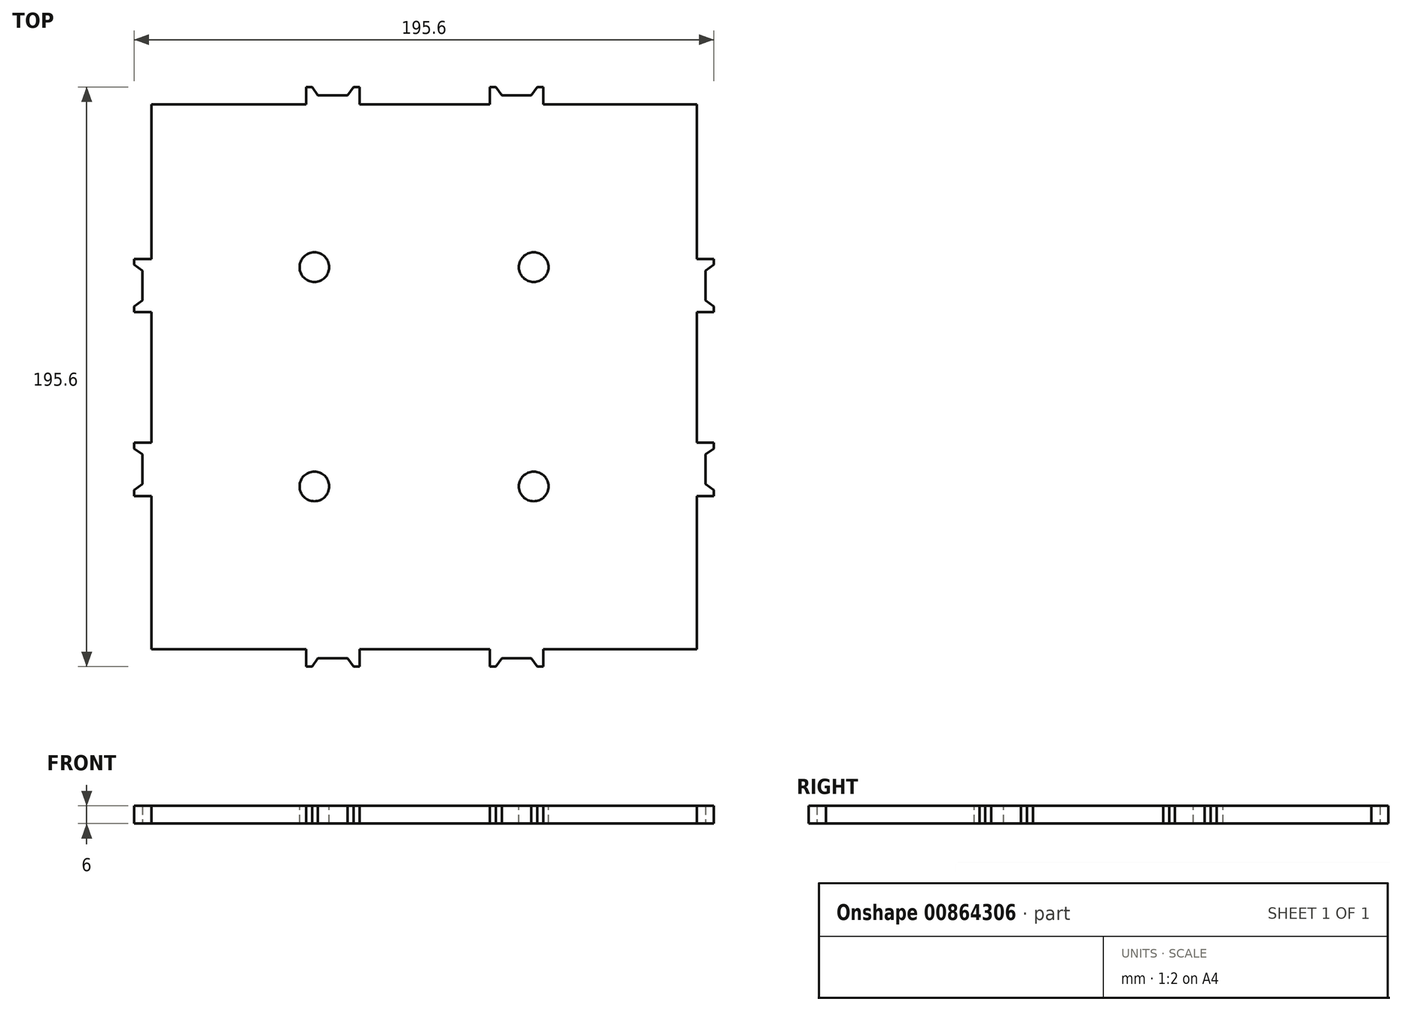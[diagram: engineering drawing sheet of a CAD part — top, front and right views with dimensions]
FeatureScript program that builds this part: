
annotation { "Feature Type Name" : "Feature", "Feature Type Description" : "" }
export const myFeature = defineFeature(function(context is Context, id is Id, definition is map)
    precondition{}
    {
        {
            var Q0;
            Q0=qCreatedBy(makeId("Top.planeOp"),FACE);
            var sketch = newSketch(context, id + "F0", { "sketchPlane" : qUnion([Q0])});
            skLineSegment(sketch, "E0.bottom", {"start": v(-124.48, 94.97) * mm, "end": v(-72.28, 94.97) * mm});
            skLineSegment(sketch, "E0.top", {"start": v(-124.48, -89.03) * mm, "end": v(-72.28, -89.03) * mm});
            skLineSegment(sketch, "E0.left", {"start": v(-124.48, 94.97) * mm, "end": v(-124.48, 42.77) * mm});
            skLineSegment(sketch, "E0.right", {"start": v(59.52, 94.97) * mm, "end": v(59.52, 42.77) * mm});
            skLineSegment(sketch, "E1", {"start": v(-72.28, 94.97) * mm, "end": v(-72.28, 100.77) * mm});
            skLineSegment(sketch, "E2", {"start": v(-72.28, 100.77) * mm, "end": v(-70.28, 100.77) * mm});
            skLineSegment(sketch, "E3", {"start": v(-70.28, 100.77) * mm, "end": v(-68.28, 97.97) * mm});
            skLineSegment(sketch, "E4", {"start": v(-68.28, 97.97) * mm, "end": v(-58.28, 97.97) * mm});
            skLineSegment(sketch, "E5", {"start": v(-58.28, 97.97) * mm, "end": v(-56.28, 100.77) * mm});
            skLineSegment(sketch, "E6", {"start": v(-56.28, 100.77) * mm, "end": v(-54.28, 100.77) * mm});
            skLineSegment(sketch, "E7", {"start": v(-54.28, 100.77) * mm, "end": v(-54.28, 94.97) * mm});
            skLineSegment(sketch, "E8.trimOffspring", {"start": v(-54.28, 94.97) * mm, "end": v(-10.28, 94.97) * mm});
            skLineSegment(sketch, "E9", {"start": v(-10.28, 94.97) * mm, "end": v(-10.28, 100.77) * mm});
            skLineSegment(sketch, "E10", {"start": v(-10.28, 100.77) * mm, "end": v(-8.28, 100.77) * mm});
            skLineSegment(sketch, "E11", {"start": v(-8.28, 100.77) * mm, "end": v(-6.28, 97.97) * mm});
            skLineSegment(sketch, "E12", {"start": v(-6.28, 97.97) * mm, "end": v(3.72, 97.97) * mm});
            skLineSegment(sketch, "E13", {"start": v(3.72, 97.97) * mm, "end": v(5.72, 100.77) * mm});
            skLineSegment(sketch, "E14", {"start": v(5.72, 100.77) * mm, "end": v(7.72, 100.77) * mm});
            skLineSegment(sketch, "E15", {"start": v(7.72, 100.77) * mm, "end": v(7.72, 94.97) * mm});
            skLineSegment(sketch, "E16.trimOffspring", {"start": v(7.72, 94.97) * mm, "end": v(59.52, 94.97) * mm});
            skLineSegment(sketch, "E17", {"start": v(59.52, 42.77) * mm, "end": v(65.32, 42.77) * mm});
            skLineSegment(sketch, "E18", {"start": v(65.32, 42.77) * mm, "end": v(65.32, 40.77) * mm});
            skLineSegment(sketch, "E19", {"start": v(65.32, 40.77) * mm, "end": v(62.52, 38.77) * mm});
            skLineSegment(sketch, "E20", {"start": v(62.52, 38.77) * mm, "end": v(62.52, 28.77) * mm});
            skLineSegment(sketch, "E21", {"start": v(62.52, 28.77) * mm, "end": v(65.32, 26.77) * mm});
            skLineSegment(sketch, "E22", {"start": v(65.32, 26.77) * mm, "end": v(65.32, 24.77) * mm});
            skLineSegment(sketch, "E23", {"start": v(65.32, 24.77) * mm, "end": v(59.52, 24.77) * mm});
            skLineSegment(sketch, "E24", {"start": v(59.52, -19.23) * mm, "end": v(65.32, -19.23) * mm});
            skLineSegment(sketch, "E25", {"start": v(65.32, -19.23) * mm, "end": v(65.32, -21.23) * mm});
            skLineSegment(sketch, "E26", {"start": v(65.32, -21.23) * mm, "end": v(62.52, -23.23) * mm});
            skLineSegment(sketch, "E27", {"start": v(62.52, -23.23) * mm, "end": v(62.52, -33.23) * mm});
            skLineSegment(sketch, "E28", {"start": v(62.52, -33.23) * mm, "end": v(65.32, -35.23) * mm});
            skLineSegment(sketch, "E29", {"start": v(65.32, -35.23) * mm, "end": v(65.32, -37.23) * mm});
            skLineSegment(sketch, "E30", {"start": v(65.32, -37.23) * mm, "end": v(59.52, -37.23) * mm});
            skLineSegment(sketch, "E31.trimOffspring", {"start": v(59.52, 24.77) * mm, "end": v(59.52, -19.23) * mm});
            skLineSegment(sketch, "E32.trimOffspring", {"start": v(59.52, -37.23) * mm, "end": v(59.52, -89.03) * mm});
            skLineSegment(sketch, "E33", {"start": v(-72.28, -89.03) * mm, "end": v(-72.28, -94.83) * mm});
            skLineSegment(sketch, "E34", {"start": v(-72.28, -94.83) * mm, "end": v(-70.28, -94.83) * mm});
            skLineSegment(sketch, "E35", {"start": v(-70.28, -94.83) * mm, "end": v(-68.28, -92.03) * mm});
            skLineSegment(sketch, "E36", {"start": v(-68.28, -92.03) * mm, "end": v(-58.28, -92.03) * mm});
            skLineSegment(sketch, "E37", {"start": v(-58.28, -92.03) * mm, "end": v(-56.28, -94.83) * mm});
            skLineSegment(sketch, "E38", {"start": v(-56.28, -94.83) * mm, "end": v(-54.28, -94.83) * mm});
            skLineSegment(sketch, "E39", {"start": v(-54.28, -94.83) * mm, "end": v(-54.28, -89.03) * mm});
            skLineSegment(sketch, "E40", {"start": v(-10.28, -89.03) * mm, "end": v(-10.28, -94.83) * mm});
            skLineSegment(sketch, "E41", {"start": v(-10.28, -94.83) * mm, "end": v(-8.28, -94.83) * mm});
            skLineSegment(sketch, "E42", {"start": v(-8.28, -94.83) * mm, "end": v(-6.28, -92.03) * mm});
            skLineSegment(sketch, "E43", {"start": v(-6.28, -92.03) * mm, "end": v(3.72, -92.03) * mm});
            skLineSegment(sketch, "E44", {"start": v(3.72, -92.03) * mm, "end": v(5.72, -94.83) * mm});
            skLineSegment(sketch, "E45", {"start": v(5.72, -94.83) * mm, "end": v(7.72, -94.83) * mm});
            skLineSegment(sketch, "E46", {"start": v(7.72, -94.83) * mm, "end": v(7.72, -89.03) * mm});
            skLineSegment(sketch, "E47.trimOffspring", {"start": v(-54.28, -89.03) * mm, "end": v(-10.28, -89.03) * mm});
            skLineSegment(sketch, "E48.trimOffspring", {"start": v(7.72, -89.03) * mm, "end": v(59.52, -89.03) * mm});
            skLineSegment(sketch, "E49", {"start": v(-124.48, 42.77) * mm, "end": v(-130.28, 42.77) * mm});
            skLineSegment(sketch, "E50", {"start": v(-130.28, 42.77) * mm, "end": v(-130.28, 40.77) * mm});
            skLineSegment(sketch, "E51", {"start": v(-130.28, 40.77) * mm, "end": v(-127.48, 38.77) * mm});
            skLineSegment(sketch, "E52", {"start": v(-127.48, 38.77) * mm, "end": v(-127.48, 28.77) * mm});
            skLineSegment(sketch, "E53", {"start": v(-127.48, 28.77) * mm, "end": v(-130.28, 26.77) * mm});
            skLineSegment(sketch, "E54", {"start": v(-130.28, 26.77) * mm, "end": v(-130.28, 24.77) * mm});
            skLineSegment(sketch, "E55", {"start": v(-130.28, 24.77) * mm, "end": v(-124.48, 24.77) * mm});
            skLineSegment(sketch, "E56", {"start": v(-124.48, -19.23) * mm, "end": v(-130.28, -19.23) * mm});
            skLineSegment(sketch, "E57", {"start": v(-130.28, -19.23) * mm, "end": v(-130.28, -21.23) * mm});
            skLineSegment(sketch, "E58", {"start": v(-130.28, -21.23) * mm, "end": v(-127.48, -23.23) * mm});
            skLineSegment(sketch, "E59", {"start": v(-127.48, -23.23) * mm, "end": v(-127.48, -33.23) * mm});
            skLineSegment(sketch, "E60", {"start": v(-127.48, -33.23) * mm, "end": v(-130.28, -35.23) * mm});
            skLineSegment(sketch, "E61", {"start": v(-130.28, -35.23) * mm, "end": v(-130.28, -37.23) * mm});
            skLineSegment(sketch, "E62", {"start": v(-130.28, -37.23) * mm, "end": v(-124.48, -37.23) * mm});
            skLineSegment(sketch, "E63.trimOffspring", {"start": v(-124.48, 24.77) * mm, "end": v(-124.48, -19.23) * mm});
            skLineSegment(sketch, "E64.trimOffspring", {"start": v(-124.48, -37.23) * mm, "end": v(-124.48, -89.03) * mm});
            skSolve(sketch);
        }
        {
            var Q0;
            Q0=makeQuery(id+"F0.imprint","IMPRINT",FACE,{"disambiguationData":[TD([[makeQuery(id+"F0.imprint","IMPRINT",EDGE,{"derivedFrom":sQuery(id+"F0.wireOp",EDGE,"E0.bottom")}),-1.0]])]});
            extrude(context, id + "F1", {"entities" : qUnion([Q0]), "depth" : 6 * mm, "offsetDistance" : 25 * mm});
        }
        {
            var Q0;
            Q0=makeQuery(id+"F1.opExtrude","CAP_FACE",FACE,{"disambiguationData":[OSD([sQuery(id+"F0.wireOp",EDGE,"E0.bottom"),sQuery(id+"F0.wireOp",EDGE,"E0.top"),sQuery(id+"F0.wireOp",EDGE,"E0.left"),sQuery(id+"F0.wireOp",EDGE,"E0.right"),sQuery(id+"F0.wireOp",EDGE,"E1"),sQuery(id+"F0.wireOp",EDGE,"E2"),sQuery(id+"F0.wireOp",EDGE,"E3"),sQuery(id+"F0.wireOp",EDGE,"E4"),sQuery(id+"F0.wireOp",EDGE,"E5"),sQuery(id+"F0.wireOp",EDGE,"E6"),sQuery(id+"F0.wireOp",EDGE,"E7"),sQuery(id+"F0.wireOp",EDGE,"E8.trimOffspring"),sQuery(id+"F0.wireOp",EDGE,"E9"),sQuery(id+"F0.wireOp",EDGE,"E10"),sQuery(id+"F0.wireOp",EDGE,"E11"),sQuery(id+"F0.wireOp",EDGE,"E12"),sQuery(id+"F0.wireOp",EDGE,"E13"),sQuery(id+"F0.wireOp",EDGE,"E14"),sQuery(id+"F0.wireOp",EDGE,"E15"),sQuery(id+"F0.wireOp",EDGE,"E16.trimOffspring"),sQuery(id+"F0.wireOp",EDGE,"E17"),sQuery(id+"F0.wireOp",EDGE,"E18"),sQuery(id+"F0.wireOp",EDGE,"E19"),sQuery(id+"F0.wireOp",EDGE,"E20"),sQuery(id+"F0.wireOp",EDGE,"E21"),sQuery(id+"F0.wireOp",EDGE,"E22"),sQuery(id+"F0.wireOp",EDGE,"E23"),sQuery(id+"F0.wireOp",EDGE,"E24"),sQuery(id+"F0.wireOp",EDGE,"E25"),sQuery(id+"F0.wireOp",EDGE,"E26"),sQuery(id+"F0.wireOp",EDGE,"E27"),sQuery(id+"F0.wireOp",EDGE,"E28"),sQuery(id+"F0.wireOp",EDGE,"E29"),sQuery(id+"F0.wireOp",EDGE,"E30"),sQuery(id+"F0.wireOp",EDGE,"E31.trimOffspring"),sQuery(id+"F0.wireOp",EDGE,"E32.trimOffspring"),sQuery(id+"F0.wireOp",EDGE,"E33"),sQuery(id+"F0.wireOp",EDGE,"E34"),sQuery(id+"F0.wireOp",EDGE,"E35"),sQuery(id+"F0.wireOp",EDGE,"E36"),sQuery(id+"F0.wireOp",EDGE,"E37"),sQuery(id+"F0.wireOp",EDGE,"E38"),sQuery(id+"F0.wireOp",EDGE,"E39"),sQuery(id+"F0.wireOp",EDGE,"E40"),sQuery(id+"F0.wireOp",EDGE,"E41"),sQuery(id+"F0.wireOp",EDGE,"E42"),sQuery(id+"F0.wireOp",EDGE,"E43"),sQuery(id+"F0.wireOp",EDGE,"E44"),sQuery(id+"F0.wireOp",EDGE,"E45"),sQuery(id+"F0.wireOp",EDGE,"E46"),sQuery(id+"F0.wireOp",EDGE,"E47.trimOffspring"),sQuery(id+"F0.wireOp",EDGE,"E48.trimOffspring"),sQuery(id+"F0.wireOp",EDGE,"E49"),sQuery(id+"F0.wireOp",EDGE,"E50"),sQuery(id+"F0.wireOp",EDGE,"E51"),sQuery(id+"F0.wireOp",EDGE,"E52"),sQuery(id+"F0.wireOp",EDGE,"E53"),sQuery(id+"F0.wireOp",EDGE,"E54"),sQuery(id+"F0.wireOp",EDGE,"E55"),sQuery(id+"F0.wireOp",EDGE,"E56"),sQuery(id+"F0.wireOp",EDGE,"E57"),sQuery(id+"F0.wireOp",EDGE,"E58"),sQuery(id+"F0.wireOp",EDGE,"E59"),sQuery(id+"F0.wireOp",EDGE,"E60"),sQuery(id+"F0.wireOp",EDGE,"E61"),sQuery(id+"F0.wireOp",EDGE,"E62"),sQuery(id+"F0.wireOp",EDGE,"E63.trimOffspring"),sQuery(id+"F0.wireOp",EDGE,"E64.trimOffspring")])],"isStart":false});
            var sketch = newSketch(context, id + "F2", { "sketchPlane" : qUnion([Q0])});
            skLineSegment(sketch, "E65", {"start": v(-124.48, 94.97) * mm, "end": v(59.52, -89.03) * mm, "construction": true});
            skLineSegment(sketch, "E66", {"start": v(-124.48, -89.03) * mm, "end": v(59.52, 94.97) * mm, "construction": true});
            skLineSegment(sketch, "E67.bottom", {"start": v(-57.48, 27.97) * mm, "end": v(-7.48, 27.97) * mm, "construction": true});
            skLineSegment(sketch, "E67.top", {"start": v(-57.48, -22.03) * mm, "end": v(-7.48, -22.03) * mm, "construction": true});
            skLineSegment(sketch, "E67.left", {"start": v(-57.48, 27.97) * mm, "end": v(-57.48, -22.03) * mm, "construction": true});
            skLineSegment(sketch, "E67.right", {"start": v(-7.48, 27.97) * mm, "end": v(-7.48, -22.03) * mm, "construction": true});
            skPoint(sketch, "E67.middle", {"position": v(-32.48, 2.97) * mm});
            skLineSegment(sketch, "E68.bottom", {"start": v(17.52, 52.97) * mm, "end": v(-82.48, 52.97) * mm, "construction": true});
            skLineSegment(sketch, "E68.top", {"start": v(17.52, -47.03) * mm, "end": v(-82.48, -47.03) * mm, "construction": true});
            skLineSegment(sketch, "E68.left", {"start": v(17.52, 52.97) * mm, "end": v(17.52, -47.03) * mm, "construction": true});
            skLineSegment(sketch, "E68.right", {"start": v(-82.48, 52.97) * mm, "end": v(-82.48, -47.03) * mm, "construction": true});
            skCircle(sketch, "E69", {"center": v(-69.48, 39.97) * mm, "radius": 5 * mm});
            skCircle(sketch, "E70", {"center": v(4.52, 39.97) * mm, "radius": 5 * mm});
            skCircle(sketch, "E71", {"center": v(-69.48, -34.03) * mm, "radius": 5 * mm});
            skCircle(sketch, "E72", {"center": v(4.52, -34.03) * mm, "radius": 5 * mm});
            skSolve(sketch);
        }
        {
            var Q0;
            Q0=makeQuery(id+"F2.imprint","IMPRINT",FACE,{"disambiguationData":[TD([[makeQuery(id+"F2.imprint","IMPRINT",EDGE,{"derivedFrom":sQuery(id+"F2.wireOp",EDGE,"E69")}),1.0]])]});
            var Q1;
            Q1=makeQuery(id+"F2.imprint","IMPRINT",FACE,{"disambiguationData":[TD([[makeQuery(id+"F2.imprint","IMPRINT",EDGE,{"derivedFrom":sQuery(id+"F2.wireOp",EDGE,"E70")}),1.0]])]});
            var Q2;
            Q2=makeQuery(id+"F2.imprint","IMPRINT",FACE,{"disambiguationData":[TD([[makeQuery(id+"F2.imprint","IMPRINT",EDGE,{"derivedFrom":sQuery(id+"F2.wireOp",EDGE,"E72")}),1.0]])]});
            var Q3;
            Q3=makeQuery(id+"F2.imprint","IMPRINT",FACE,{"disambiguationData":[TD([[makeQuery(id+"F2.imprint","IMPRINT",EDGE,{"derivedFrom":sQuery(id+"F2.wireOp",EDGE,"E71")}),1.0]])]});
            extrude(context, id + "F3", {"entities" : qUnion([Q0, Q1, Q2, Q3]), "operationType" : NewBodyOperationType.REMOVE, "oppositeDirection" : true, "depth" : 6 * mm, "offsetDistance" : 25 * mm});
        }
    });
